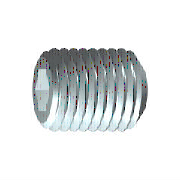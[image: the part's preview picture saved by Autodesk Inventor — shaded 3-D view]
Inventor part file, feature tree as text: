
AUTODESK INVENTOR PART (.ipt)
format: ipt  version: 2014 (Build 180170000, 170)  size: 168,448 bytes
history: native  units: mm (DEFAULTED — no unit token found)
features: sketch x2, extrude x1, other x1, plane x1
ambient origin geometry x8: Origin, YZ Plane, XZ Plane, XY Plane, X Axis, Y Axis, Z Axis, Center Point
bodies: Solid1 (feature_tree), Body (feature_tree)
feature tree (5):
  extrude  "Slot"  TaperAngle=60.0deg  [1 undecoded]
  other  "Work Axis1"
  plane  "Work Plane1"
  sketch  "Sketch1"  dims[d0=2.286mm d1=60.0deg]
  sketch  "Sketch2"  dims[d2=4.1656mm d3=2.287693mm d6=90.0deg d4=0.0mm d5=4.826mm d7=0.486914mm d8=45.0deg d21=10.0mm d9=0.0mm d11=4.826mm d12=0.0mm d13=0.486914mm d14=45.0deg d15=0.0mm d29=0.486914mm d30=0.486914mm d31=0.0mm]
note: 1 required parameter value undecoded (feature->parameter linkage not recoverable at this tier; creation-order binding heuristic only, values carry confidence <= 0.55)
